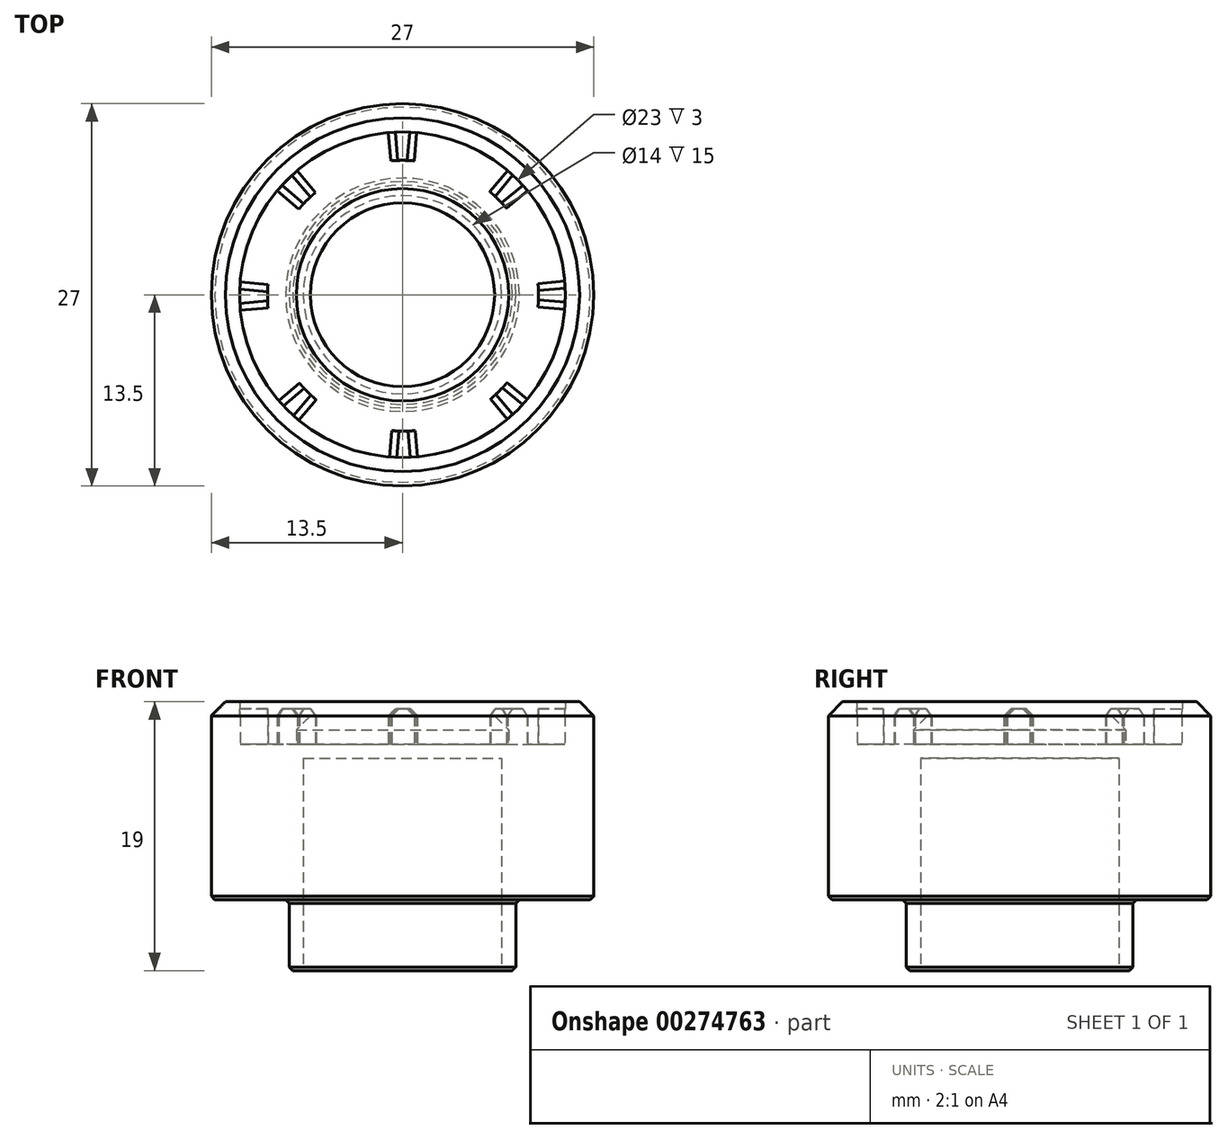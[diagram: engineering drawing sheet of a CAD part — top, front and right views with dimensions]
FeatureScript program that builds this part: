
annotation { "Feature Type Name" : "Feature", "Feature Type Description" : "" }
export const myFeature = defineFeature(function(context is Context, id is Id, definition is map)
    precondition{}
    {
        {
            var Q0;
            Q0=qCreatedBy(makeId("Front.planeOp"),FACE);
            var sketch = newSketch(context, id + "F0", { "sketchPlane" : qUnion([Q0])});
            skLineSegment(sketch, "E0", {"start": v(7, 0) * mm, "end": v(7, 15) * mm});
            skLineSegment(sketch, "E1", {"start": v(7, 15) * mm, "end": v(0, 15) * mm});
            skLineSegment(sketch, "E2", {"start": v(0, 15) * mm, "end": v(0, 18) * mm});
            skLineSegment(sketch, "E3", {"start": v(0, 18) * mm, "end": v(7.5, 18) * mm});
            skLineSegment(sketch, "E4", {"start": v(7.5, 18) * mm, "end": v(7.5, 16) * mm});
            skLineSegment(sketch, "E5", {"start": v(7.5, 16) * mm, "end": v(11.5, 16) * mm});
            skLineSegment(sketch, "E6", {"start": v(11.5, 16) * mm, "end": v(11.5, 19) * mm});
            skLineSegment(sketch, "E7", {"start": v(11.5, 19) * mm, "end": v(13.5, 19) * mm});
            skLineSegment(sketch, "E8", {"start": v(13.5, 19) * mm, "end": v(13.5, 5) * mm});
            skLineSegment(sketch, "E9", {"start": v(13.5, 5) * mm, "end": v(8, 5) * mm});
            skLineSegment(sketch, "E10", {"start": v(8, 5) * mm, "end": v(8, 0) * mm});
            skLineSegment(sketch, "E11", {"start": v(8, 0) * mm, "end": v(7, 0) * mm});
            skSolve(sketch);
        }
        {
            var Q0;
            Q0 = qSketchRegion(id + "F0", true);
            var Q1;
            Q1=sQuery(id+"F0.wireOp",EDGE,"E2");
            revolve(context, id + "F1", {"entities" : qUnion([Q0]), "axis" : qUnion([Q1]), "revolveType" : RevolveType.FULL});
        }
        {
            var Q0;
            Q0=makeQuery(id+"F1.opRevolve","SWEPT_FACE",FACE,{"disambiguationData":[OSD([sQuery(id+"F0.wireOp",EDGE,"E5")])]});
            var sketch = newSketch(context, id + "F2", { "sketchPlane" : qUnion([Q0])});
            skArc(sketch, "E12.0", {"start": v(1, 11.46) * mm, "mid": v(0, 11.5) * mm, "end": v(-1, 11.46) * mm});
            skLineSegment(sketch, "E13", {"start": v(0.83, 9.46) * mm, "end": v(1, 11.46) * mm});
            skLineSegment(sketch, "E14", {"start": v(-0.83, 9.46) * mm, "end": v(-1, 11.46) * mm});
            skArc(sketch, "E15.0", {"start": v(0.83, 9.46) * mm, "mid": v(0, 9.5) * mm, "end": v(-0.83, 9.46) * mm});
            skArc(sketch, "E16.1.0", {"start": v(-7.43, 8.76) * mm, "mid": v(-8.17, 8.09) * mm, "end": v(-8.85, 7.35) * mm});
            skLineSegment(sketch, "E16.1.1", {"start": v(-7.31, 6.06) * mm, "end": v(-8.85, 7.35) * mm});
            skLineSegment(sketch, "E16.1.2", {"start": v(-6.14, 7.23) * mm, "end": v(-7.43, 8.76) * mm});
            skArc(sketch, "E16.1.3", {"start": v(-6.14, 7.23) * mm, "mid": v(-6.75, 6.67) * mm, "end": v(-7.31, 6.06) * mm});
            skArc(sketch, "E16.2.0", {"start": v(-11.49, 0.9) * mm, "mid": v(-11.53, -0.1) * mm, "end": v(-11.49, -1.1) * mm});
            skLineSegment(sketch, "E16.2.1", {"start": v(-9.5, -0.93) * mm, "end": v(-11.49, -1.1) * mm});
            skLineSegment(sketch, "E16.2.2", {"start": v(-9.5, 0.73) * mm, "end": v(-11.49, 0.9) * mm});
            skArc(sketch, "E16.2.3", {"start": v(-9.5, 0.73) * mm, "mid": v(-9.53, -0.1) * mm, "end": v(-9.5, -0.93) * mm});
            skArc(sketch, "E16.3.0", {"start": v(-8.8, -7.53) * mm, "mid": v(-8.12, -8.27) * mm, "end": v(-7.38, -8.95) * mm});
            skLineSegment(sketch, "E16.3.1", {"start": v(-6.1, -7.42) * mm, "end": v(-7.38, -8.95) * mm});
            skLineSegment(sketch, "E16.3.2", {"start": v(-7.26, -6.25) * mm, "end": v(-8.8, -7.53) * mm});
            skArc(sketch, "E16.3.3", {"start": v(-7.26, -6.25) * mm, "mid": v(-6.7, -6.86) * mm, "end": v(-6.1, -7.42) * mm});
            skArc(sketch, "E16.4.0", {"start": v(-0.93, -11.59) * mm, "mid": v(0.07, -11.63) * mm, "end": v(1.07, -11.59) * mm});
            skLineSegment(sketch, "E16.4.1", {"start": v(0.9, -9.6) * mm, "end": v(1.07, -11.59) * mm});
            skLineSegment(sketch, "E16.4.2", {"start": v(-0.76, -9.6) * mm, "end": v(-0.93, -11.59) * mm});
            skArc(sketch, "E16.4.3", {"start": v(-0.76, -9.6) * mm, "mid": v(0.07, -9.63) * mm, "end": v(0.9, -9.6) * mm});
            skArc(sketch, "E16.5.0", {"start": v(7.5, -8.9) * mm, "mid": v(8.24, -8.22) * mm, "end": v(8.92, -7.48) * mm});
            skLineSegment(sketch, "E16.5.1", {"start": v(7.39, -6.2) * mm, "end": v(8.92, -7.48) * mm});
            skLineSegment(sketch, "E16.5.2", {"start": v(6.21, -7.37) * mm, "end": v(7.5, -8.9) * mm});
            skArc(sketch, "E16.5.3", {"start": v(6.21, -7.37) * mm, "mid": v(6.83, -6.8) * mm, "end": v(7.39, -6.2) * mm});
            skArc(sketch, "E16.6.0", {"start": v(11.56, -1.03) * mm, "mid": v(11.6, -0.03) * mm, "end": v(11.56, 0.97) * mm});
            skLineSegment(sketch, "E16.6.1", {"start": v(9.57, 0.8) * mm, "end": v(11.56, 0.97) * mm});
            skLineSegment(sketch, "E16.6.2", {"start": v(9.57, -0.86) * mm, "end": v(11.56, -1.03) * mm});
            skArc(sketch, "E16.6.3", {"start": v(9.57, -0.86) * mm, "mid": v(9.6, -0.03) * mm, "end": v(9.57, 0.8) * mm});
            skArc(sketch, "E16.7.0", {"start": v(8.87, 7.4) * mm, "mid": v(8.19, 8.14) * mm, "end": v(7.45, 8.82) * mm});
            skLineSegment(sketch, "E16.7.1", {"start": v(6.16, 7.28) * mm, "end": v(7.45, 8.82) * mm});
            skLineSegment(sketch, "E16.7.2", {"start": v(7.34, 6.11) * mm, "end": v(8.87, 7.4) * mm});
            skArc(sketch, "E16.7.3", {"start": v(7.34, 6.11) * mm, "mid": v(6.78, 6.72) * mm, "end": v(6.16, 7.28) * mm});
            skPoint(sketch, "E16.center", {"position": v(0.04, -0.07) * mm});
            skSolve(sketch);
        }
        {
            var Q0;
            Q0=makeQuery(id+"F2.imprint","IMPRINT",FACE,{"disambiguationData":[TD([[makeQuery(id+"F2.imprint","IMPRINT",EDGE,{"derivedFrom":sQuery(id+"F2.wireOp",EDGE,"E12.0")}),-1.0]])]});
            var Q1;
            {var subQ0=sQuery(id+"F2.wireOp",EDGE,"E16.11.3");Q1=makeQuery(id+"F2.imprint","IMPRINT",FACE,{"disambiguationData":[TD([[makeQuery(id+"F2.imprint","IMPRINT",EDGE,{"derivedFrom":subQ0}),-1.0]])]});}
            var Q2;
            {var subQ0=sQuery(id+"F2.wireOp",EDGE,"E16.10.3");Q2=makeQuery(id+"F2.imprint","IMPRINT",FACE,{"disambiguationData":[TD([[makeQuery(id+"F2.imprint","IMPRINT",EDGE,{"derivedFrom":subQ0}),-1.0]])]});}
            var Q3;
            {var subQ0=sQuery(id+"F2.wireOp",EDGE,"E16.9.3");Q3=makeQuery(id+"F2.imprint","IMPRINT",FACE,{"disambiguationData":[TD([[makeQuery(id+"F2.imprint","IMPRINT",EDGE,{"derivedFrom":subQ0}),-1.0]])]});}
            var Q4;
            {var subQ0=sQuery(id+"F2.wireOp",EDGE,"E16.8.3");Q4=makeQuery(id+"F2.imprint","IMPRINT",FACE,{"disambiguationData":[TD([[makeQuery(id+"F2.imprint","IMPRINT",EDGE,{"derivedFrom":subQ0}),-1.0]])]});}
            var Q5;
            {var subQ0=sQuery(id+"F2.wireOp",EDGE,"E16.7.3");Q5=makeQuery(id+"F2.imprint","IMPRINT",FACE,{"disambiguationData":[TD([[makeQuery(id+"F2.imprint","IMPRINT",EDGE,{"derivedFrom":subQ0}),-1.0]])]});}
            var Q6;
            {var subQ0=sQuery(id+"F2.wireOp",EDGE,"E16.6.3");Q6=makeQuery(id+"F2.imprint","IMPRINT",FACE,{"disambiguationData":[TD([[makeQuery(id+"F2.imprint","IMPRINT",EDGE,{"derivedFrom":subQ0}),-1.0]])]});}
            var Q7;
            {var subQ0=sQuery(id+"F2.wireOp",EDGE,"E16.5.3");Q7=makeQuery(id+"F2.imprint","IMPRINT",FACE,{"disambiguationData":[TD([[makeQuery(id+"F2.imprint","IMPRINT",EDGE,{"derivedFrom":subQ0}),-1.0]])]});}
            var Q8;
            {var subQ0=sQuery(id+"F2.wireOp",EDGE,"E16.4.3");Q8=makeQuery(id+"F2.imprint","IMPRINT",FACE,{"disambiguationData":[TD([[makeQuery(id+"F2.imprint","IMPRINT",EDGE,{"derivedFrom":subQ0}),-1.0]])]});}
            var Q9;
            {var subQ0=sQuery(id+"F2.wireOp",EDGE,"E16.3.3");Q9=makeQuery(id+"F2.imprint","IMPRINT",FACE,{"disambiguationData":[TD([[makeQuery(id+"F2.imprint","IMPRINT",EDGE,{"derivedFrom":subQ0}),-1.0]])]});}
            var Q10;
            {var subQ1=sQuery(id+"F2.wireOp",EDGE,"E16.2.2");Q10=makeQuery(id+"F2.imprint","IMPRINT",FACE,{"disambiguationData":[TD([[makeQuery(id+"F2.imprint","IMPRINT",EDGE,{"derivedFrom":subQ1}),1.0]])]});}
            var Q11;
            Q11=makeQuery(id+"F2.imprint","IMPRINT",FACE,{"disambiguationData":[TD([[makeQuery(id+"F2.imprint","IMPRINT",EDGE,{"derivedFrom":sQuery(id+"F2.wireOp",EDGE,"E16.1.0")}),1.0]])]});
            extrude(context, id + "F3", {"entities" : qUnion([Q0, Q1, Q2, Q3, Q4, Q5, Q6, Q7, Q8, Q9, Q10, Q11]), "operationType" : NewBodyOperationType.ADD, "depth" : 2.5 * mm});
        }
        {
            var Q0;
            Q0=makeQuery(id+"F1.opRevolve","SWEPT_EDGE",EDGE,{"disambiguationData":[OSD([sQuery(id+"F0.wireOp",EDGE,"E7"),sQuery(id+"F0.wireOp",EDGE,"E8")])]});
            var Q1;
            Q1=makeQuery(id+"F1.opRevolve","SWEPT_EDGE",EDGE,{"disambiguationData":[OSD([sQuery(id+"F0.wireOp",EDGE,"E3"),sQuery(id+"F0.wireOp",EDGE,"E4")])]});
            chamfer(context, id + "F4", {"entities" : qUnion([Q0, Q1]), "width" : 1 * mm, "tangentPropagation" : true});
        }
        {
            var Q0;
            Q0=makeQuery(id+"F3.opExtrude","CAP_EDGE",EDGE,{"disambiguationData":[OSD([sQuery(id+"F2.wireOp",EDGE,"E16.2.1")])],"isStart":false});
            var Q1;
            Q1=makeQuery(id+"F3.opExtrude","CAP_EDGE",EDGE,{"disambiguationData":[OSD([sQuery(id+"F2.wireOp",EDGE,"E16.2.2")])],"isStart":false});
            var Q2;
            Q2=makeQuery(id+"F3.opExtrude","CAP_EDGE",EDGE,{"disambiguationData":[OSD([sQuery(id+"F2.wireOp",EDGE,"E16.1.1")])],"isStart":false});
            var Q3;
            Q3=makeQuery(id+"F3.opExtrude","CAP_EDGE",EDGE,{"disambiguationData":[OSD([sQuery(id+"F2.wireOp",EDGE,"E16.1.2")])],"isStart":false});
            var Q4;
            Q4=makeQuery(id+"F3.opExtrude","CAP_EDGE",EDGE,{"disambiguationData":[OSD([sQuery(id+"F2.wireOp",EDGE,"E14")])],"isStart":false});
            var Q5;
            Q5=makeQuery(id+"F3.opExtrude","CAP_EDGE",EDGE,{"disambiguationData":[OSD([sQuery(id+"F2.wireOp",EDGE,"E13")])],"isStart":false});
            var Q6;
            Q6=makeQuery(id+"F3.opExtrude","CAP_EDGE",EDGE,{"disambiguationData":[OSD([sQuery(id+"F2.wireOp",EDGE,"E16.11.1")])],"isStart":false});
            var Q7;
            Q7=makeQuery(id+"F3.opExtrude","CAP_EDGE",EDGE,{"disambiguationData":[OSD([sQuery(id+"F2.wireOp",EDGE,"E16.11.2")])],"isStart":false});
            var Q8;
            Q8=makeQuery(id+"F3.opExtrude","CAP_EDGE",EDGE,{"disambiguationData":[OSD([sQuery(id+"F2.wireOp",EDGE,"E16.10.1")])],"isStart":false});
            var Q9;
            Q9=makeQuery(id+"F3.opExtrude","CAP_EDGE",EDGE,{"disambiguationData":[OSD([sQuery(id+"F2.wireOp",EDGE,"E16.10.2")])],"isStart":false});
            var Q10;
            Q10=makeQuery(id+"F3.opExtrude","CAP_EDGE",EDGE,{"disambiguationData":[OSD([sQuery(id+"F2.wireOp",EDGE,"E16.9.1")])],"isStart":false});
            var Q11;
            Q11=makeQuery(id+"F3.opExtrude","CAP_EDGE",EDGE,{"disambiguationData":[OSD([sQuery(id+"F2.wireOp",EDGE,"E16.9.2")])],"isStart":false});
            var Q12;
            Q12=makeQuery(id+"F3.opExtrude","CAP_EDGE",EDGE,{"disambiguationData":[OSD([sQuery(id+"F2.wireOp",EDGE,"E16.8.1")])],"isStart":false});
            var Q13;
            Q13=makeQuery(id+"F3.opExtrude","CAP_EDGE",EDGE,{"disambiguationData":[OSD([sQuery(id+"F2.wireOp",EDGE,"E16.8.2")])],"isStart":false});
            var Q14;
            Q14=makeQuery(id+"F3.opExtrude","CAP_EDGE",EDGE,{"disambiguationData":[OSD([sQuery(id+"F2.wireOp",EDGE,"E16.3.1")])],"isStart":false});
            var Q15;
            Q15=makeQuery(id+"F3.opExtrude","CAP_EDGE",EDGE,{"disambiguationData":[OSD([sQuery(id+"F2.wireOp",EDGE,"E16.3.2")])],"isStart":false});
            var Q16;
            Q16=makeQuery(id+"F3.opExtrude","CAP_EDGE",EDGE,{"disambiguationData":[OSD([sQuery(id+"F2.wireOp",EDGE,"E16.4.1")])],"isStart":false});
            var Q17;
            Q17=makeQuery(id+"F3.opExtrude","CAP_EDGE",EDGE,{"disambiguationData":[OSD([sQuery(id+"F2.wireOp",EDGE,"E16.4.2")])],"isStart":false});
            var Q18;
            Q18=makeQuery(id+"F3.opExtrude","CAP_EDGE",EDGE,{"disambiguationData":[OSD([sQuery(id+"F2.wireOp",EDGE,"E16.5.1")])],"isStart":false});
            var Q19;
            Q19=makeQuery(id+"F3.opExtrude","CAP_EDGE",EDGE,{"disambiguationData":[OSD([sQuery(id+"F2.wireOp",EDGE,"E16.5.2")])],"isStart":false});
            var Q20;
            Q20=makeQuery(id+"F3.opExtrude","CAP_EDGE",EDGE,{"disambiguationData":[OSD([sQuery(id+"F2.wireOp",EDGE,"E16.6.1")])],"isStart":false});
            var Q21;
            Q21=makeQuery(id+"F3.opExtrude","CAP_EDGE",EDGE,{"disambiguationData":[OSD([sQuery(id+"F2.wireOp",EDGE,"E16.6.2")])],"isStart":false});
            var Q22;
            Q22=makeQuery(id+"F3.opExtrude","CAP_EDGE",EDGE,{"disambiguationData":[OSD([sQuery(id+"F2.wireOp",EDGE,"E16.7.2")])],"isStart":false});
            var Q23;
            Q23=makeQuery(id+"F3.opExtrude","CAP_EDGE",EDGE,{"disambiguationData":[OSD([sQuery(id+"F2.wireOp",EDGE,"E16.7.1")])],"isStart":false});
            chamfer(context, id + "F5", {"entities" : qUnion([Q0, Q1, Q2, Q3, Q4, Q5, Q6, Q7, Q8, Q9, Q10, Q11, Q12, Q13, Q14, Q15, Q16, Q17, Q18, Q19, Q20, Q21, Q22, Q23]), "width" : 0.5 * mm, "tangentPropagation" : true});
        }
        {
            var Q0;
            Q0=makeQuery(id+"F1.opRevolve","SWEPT_EDGE",EDGE,{"disambiguationData":[OSD([sQuery(id+"F0.wireOp",EDGE,"E8"),sQuery(id+"F0.wireOp",EDGE,"E9")])]});
            var Q1;
            Q1=makeQuery(id+"F1.opRevolve","SWEPT_EDGE",EDGE,{"disambiguationData":[OSD([sQuery(id+"F0.wireOp",EDGE,"E9"),sQuery(id+"F0.wireOp",EDGE,"E10")])]});
            var Q2;
            Q2=makeQuery(id+"F1.opRevolve","SWEPT_EDGE",EDGE,{"disambiguationData":[OSD([sQuery(id+"F0.wireOp",EDGE,"E10"),sQuery(id+"F0.wireOp",EDGE,"E11")])]});
            chamfer(context, id + "F6", {"entities" : qUnion([Q0, Q1, Q2]), "width" : 0.25 * mm, "tangentPropagation" : true});
        }
    });
